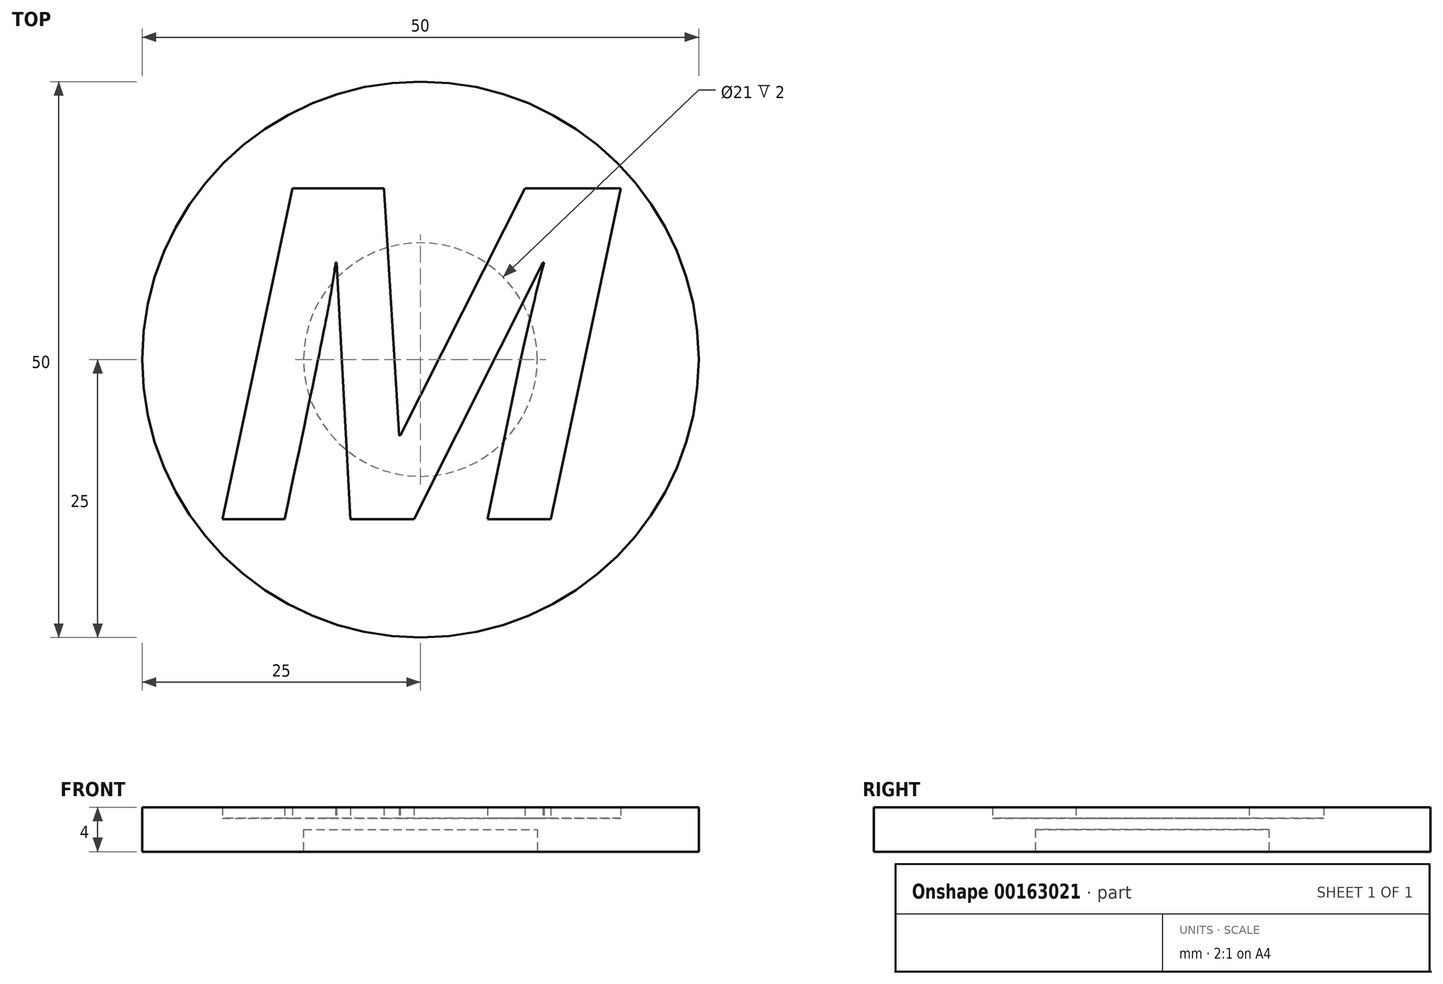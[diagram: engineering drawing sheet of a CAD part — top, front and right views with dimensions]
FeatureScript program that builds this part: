
annotation { "Feature Type Name" : "Feature", "Feature Type Description" : "" }
export const myFeature = defineFeature(function(context is Context, id is Id, definition is map)
    precondition{}
    {
        {
            var Q0;
            Q0=qCreatedBy(makeId("Top.planeOp"),FACE);
            var sketch = newSketch(context, id + "F0", { "sketchPlane" : qUnion([Q0])});
            skCircle(sketch, "E0", {"center": v(0, 0) * mm, "radius": 25 * mm});
            skText(sketch, "E1", { "text": "M", "fontName": "OpenSans-BoldItalic.ttf"});
            const initialGuessF0  = {"E1": [-0.01887, -0.01434, 1, 0, 0.03]};
            skSetInitialGuess(sketch, initialGuessF0);
            skSolve(sketch);
        }
        {
            var Q0;
            Q0=makeQuery(id+"F0.imprint","IMPRINT",FACE,{"disambiguationData":[TD([[makeQuery(id+"F0.imprint","IMPRINT",EDGE,{"derivedFrom":sQuery(id+"F0.wireOp",EDGE,"E0")}),1.0]])]});
            extrude(context, id + "F1", {"entities" : qUnion([Q0]), "depth" : 4 * mm});
        }
        {
            var Q0;
            Q0=makeQuery(id+"F0.imprint","IMPRINT",FACE,{"disambiguationData":[TD([[makeQuery(id+"F0.imprint","IMPRINT",EDGE,{"derivedFrom":sQuery(id+"F0.wireOp",EDGE,"E1.sketch_text.stroke-0")}),-1.0]])]});
            extrude(context, id + "F2", {"entities" : qUnion([Q0]), "operationType" : NewBodyOperationType.ADD, "depth" : 3 * mm});
        }
        {
            var Q0;
            {var subQ0=sQuery(id+"F0.wireOp",EDGE,"E1.sketch_text.stroke-17");var subQ1=sQuery(id+"F0.wireOp",EDGE,"E1.sketch_text.stroke-16");var subQ2=sQuery(id+"F0.wireOp",EDGE,"E1.sketch_text.stroke-15");var subQ3=sQuery(id+"F0.wireOp",EDGE,"E1.sketch_text.stroke-14");var subQ4=sQuery(id+"F0.wireOp",EDGE,"E1.sketch_text.stroke-13");var subQ5=sQuery(id+"F0.wireOp",EDGE,"E1.sketch_text.stroke-12");var subQ6=sQuery(id+"F0.wireOp",EDGE,"E1.sketch_text.stroke-11");var subQ7=sQuery(id+"F0.wireOp",EDGE,"E1.sketch_text.stroke-10");var subQ8=sQuery(id+"F0.wireOp",EDGE,"E1.sketch_text.stroke-9");var subQ9=sQuery(id+"F0.wireOp",EDGE,"E1.sketch_text.stroke-8");var subQ10=sQuery(id+"F0.wireOp",EDGE,"E1.sketch_text.stroke-7");var subQ11=sQuery(id+"F0.wireOp",EDGE,"E1.sketch_text.stroke-6");var subQ12=sQuery(id+"F0.wireOp",EDGE,"E1.sketch_text.stroke-5");var subQ13=sQuery(id+"F0.wireOp",EDGE,"E1.sketch_text.stroke-4");var subQ14=sQuery(id+"F0.wireOp",EDGE,"E1.sketch_text.stroke-3");var subQ15=sQuery(id+"F0.wireOp",EDGE,"E1.sketch_text.stroke-2");var subQ16=sQuery(id+"F0.wireOp",EDGE,"E1.sketch_text.stroke-1");var subQ17=sQuery(id+"F0.wireOp",EDGE,"E1.sketch_text.stroke-0");Q0=makeQuery(id+"F2.boolean.opBoolean","MERGE",FACE,{"derivedFrom":[makeQuery(id+"F1.opExtrude","CAP_FACE",FACE,{"disambiguationData":[OSD([sQuery(id+"F0.wireOp",EDGE,"E0"),subQ17,subQ16,subQ15,subQ14,subQ13,subQ12,subQ11,subQ10,subQ9,subQ8,subQ7,subQ6,subQ5,subQ4,subQ3,subQ2,subQ1,subQ0])],"isStart":true}),makeQuery(id+"F2.opExtrude","CAP_FACE",FACE,{"disambiguationData":[OSD([subQ17,subQ16,subQ15,subQ14,subQ13,subQ12,subQ11,subQ10,subQ9,subQ8,subQ7,subQ6,subQ5,subQ4,subQ3,subQ2,subQ1,subQ0])],"isStart":true})]});}
            var sketch = newSketch(context, id + "F3", { "sketchPlane" : qUnion([Q0])});
            skCircle(sketch, "E2", {"center": v(0, 0) * mm, "radius": 10.5 * mm});
            skSolve(sketch);
        }
        {
            var Q0;
            Q0=makeQuery(id+"F3.imprint","IMPRINT",FACE,{"disambiguationData":[TD([[makeQuery(id+"F3.imprint","IMPRINT",EDGE,{"derivedFrom":sQuery(id+"F3.wireOp",EDGE,"E2")}),1.0]])]});
            extrude(context, id + "F4", {"entities" : qUnion([Q0]), "operationType" : NewBodyOperationType.REMOVE, "oppositeDirection" : true, "depth" : 2 * mm});
        }
    });
